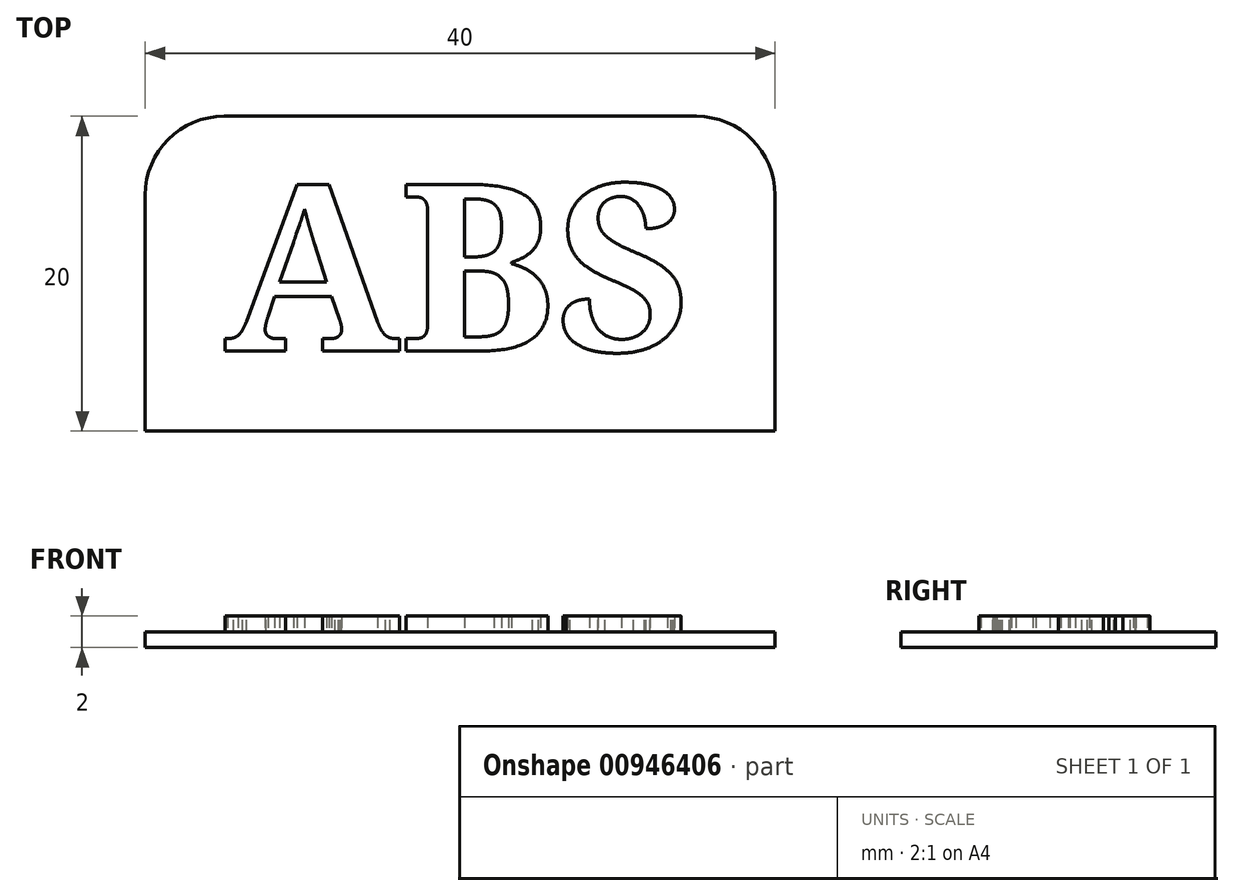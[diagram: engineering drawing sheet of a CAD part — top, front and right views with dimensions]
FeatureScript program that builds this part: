
annotation { "Feature Type Name" : "Feature", "Feature Type Description" : "" }
export const myFeature = defineFeature(function(context is Context, id is Id, definition is map)
    precondition{}
    {
        {
            var Q0;
            Q0=qCreatedBy(makeId("Top.planeOp"),FACE);
            var sketch = newSketch(context, id + "F0", { "sketchPlane" : qUnion([Q0])});
            skLineSegment(sketch, "E0.bottom", {"start": v(-20, 10) * mm, "end": v(20, 10) * mm});
            skLineSegment(sketch, "E0.top", {"start": v(-20, -10) * mm, "end": v(20, -10) * mm});
            skLineSegment(sketch, "E0.left", {"start": v(-20, 10) * mm, "end": v(-20, -10) * mm});
            skLineSegment(sketch, "E0.right", {"start": v(20, 10) * mm, "end": v(20, -10) * mm});
            skPoint(sketch, "E0.middle", {"position": v(0, 0) * mm});
            skSolve(sketch);
        }
        {
            var Q0;
            Q0=makeQuery(id+"F0.imprint","IMPRINT",FACE,{"disambiguationData":[TD([[makeQuery(id+"F0.imprint","IMPRINT",EDGE,{"derivedFrom":sQuery(id+"F0.wireOp",EDGE,"E0.bottom")}),-1.0]])]});
            extrude(context, id + "F1", {"entities" : qUnion([Q0]), "depth" : 1 * mm, "offsetDistance" : 25 * mm});
        }
        {
            var Q0;
            Q0=makeQuery(id+"F1.opExtrude","CAP_FACE",FACE,{"disambiguationData":[OSD([sQuery(id+"F0.wireOp",EDGE,"E0.bottom"),sQuery(id+"F0.wireOp",EDGE,"E0.top"),sQuery(id+"F0.wireOp",EDGE,"E0.left"),sQuery(id+"F0.wireOp",EDGE,"E0.right")])],"isStart":false});
            var sketch = newSketch(context, id + "F2", { "sketchPlane" : qUnion([Q0])});
            skText(sketch, "E1", { "text": "ABS", "fontName": "NotoSerif-Bold.ttf"});
            const initialGuessF2  = {"E1": [-0.015, -0.00491, 1, 0, 0.01066]};
            skSetInitialGuess(sketch, initialGuessF2);
            skSolve(sketch);
        }
        {
            var Q0;
            Q0=qSketchRegion(id+"F2",true);
            extrude(context, id + "F3", {"entities" : qUnion([Q0]), "operationType" : NewBodyOperationType.ADD, "depth" : 1 * mm, "offsetDistance" : 25 * mm});
        }
        {
            var Q0;
            Q0=makeQuery(id+"F1.opExtrude","SWEPT_EDGE",EDGE,{"disambiguationData":[OSD([sQuery(id+"F0.wireOp",EDGE,"E0.bottom"),sQuery(id+"F0.wireOp",EDGE,"E0.left")])]});
            var Q1;
            Q1=makeQuery(id+"F1.opExtrude","SWEPT_EDGE",EDGE,{"disambiguationData":[OSD([sQuery(id+"F0.wireOp",EDGE,"E0.bottom"),sQuery(id+"F0.wireOp",EDGE,"E0.right")])]});
            fillet(context, id + "F4", {"entities" : qUnion([Q0, Q1]), "radius" : 5 * mm, "tangentPropagation" : true, "allowEdgeOverflow" : false});
        }
    });
